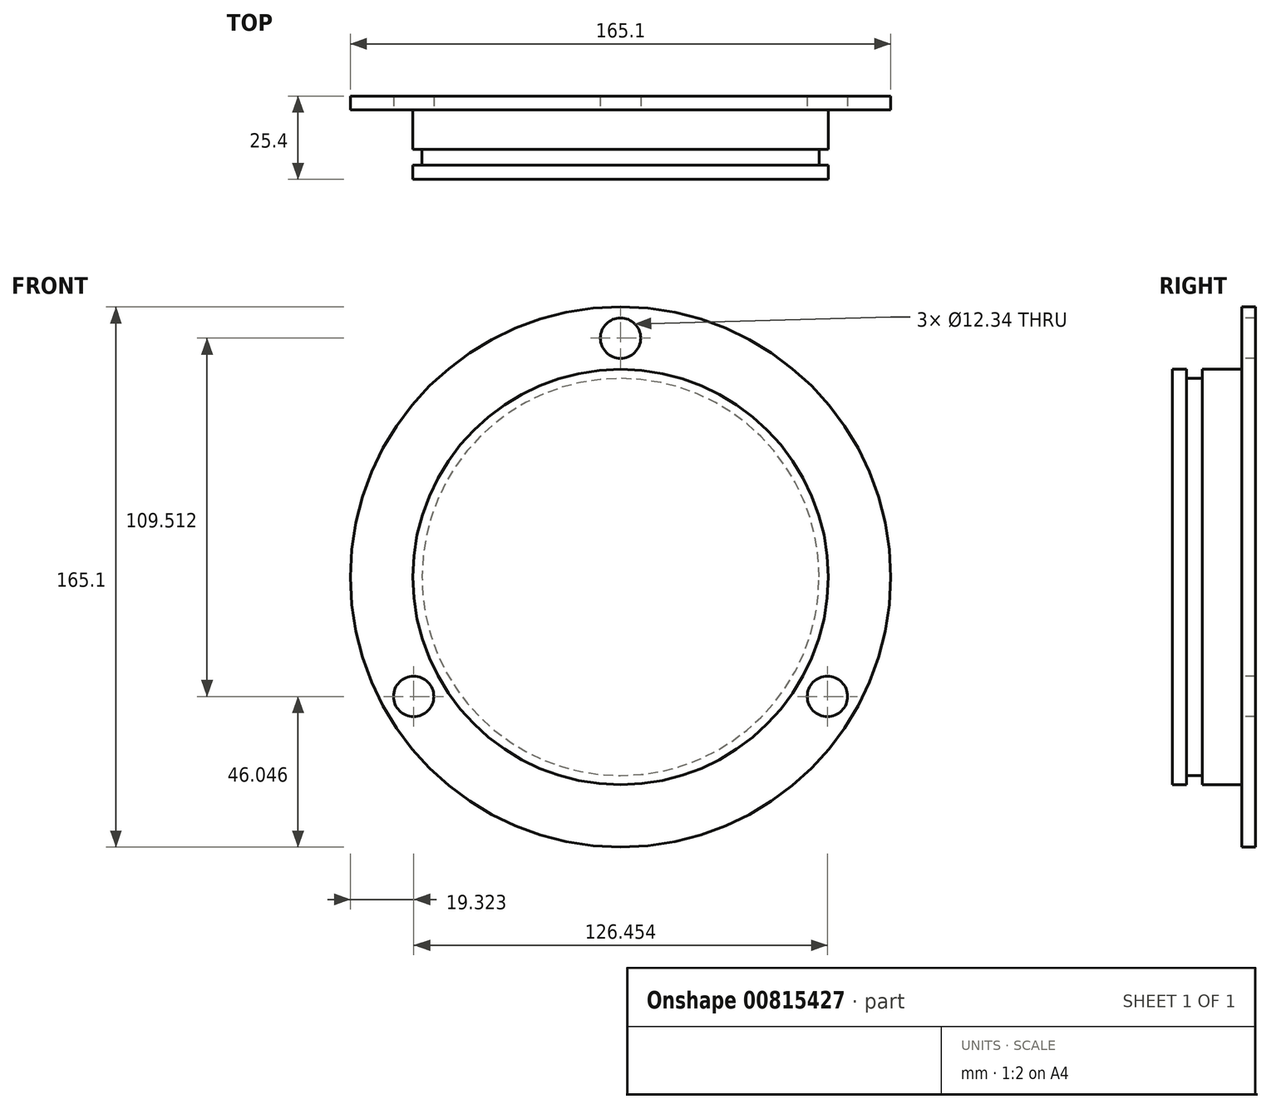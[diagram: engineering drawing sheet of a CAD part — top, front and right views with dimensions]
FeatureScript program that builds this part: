
annotation { "Feature Type Name" : "Feature", "Feature Type Description" : "" }
export const myFeature = defineFeature(function(context is Context, id is Id, definition is map)
    precondition{}
    {
        {
            var Q0;
            Q0=qCreatedBy(makeId("Front.planeOp"),FACE);
            var sketch = newSketch(context, id + "F0", { "sketchPlane" : qUnion([Q0])});
            skCircle(sketch, "E0", {"center": v(0, 0) * mm, "radius": 63.46 * mm});
            skSolve(sketch);
        }
        {
            var Q0;
            Q0=makeQuery(id+"F0.imprint","IMPRINT",FACE,{"disambiguationData":[TD([[makeQuery(id+"F0.imprint","IMPRINT",EDGE,{"derivedFrom":sQuery(id+"F0.wireOp",EDGE,"E0")}),1.0]])]});
            var Q1;
            Q1=sQuery(id+"F0.wireOp",EDGE,"E0");
            extrude(context, id + "F1", {"entities" : qUnion([Q0]), "surfaceEntities" : qUnion([Q1]), "depth" : 25.4 * mm, "offsetDistance" : 25.4 * mm});
        }
        {
            var Q0;
            Q0=makeQuery(id+"F1.opExtrude","SWEPT_BODY",BODY,{"disambiguationData":[OSD([sQuery(id+"F0.wireOp",EDGE,"E0")])]});
            var Q1;
            Q1=makeQuery(id+"F1.opExtrude","SWEPT_FACE",FACE,{"disambiguationData":[OSD([sQuery(id+"F0.wireOp",EDGE,"E0")])]});
            transform(context, id + "F2", {"entities" : qUnion([Q0]), "transformType" : TransformType.TRANSLATION_DISTANCE, "transformDirection" : qUnion([Q1]), "distance" : 27.79 * mm, "oppositeDirection" : true, "makeCopy" : false});
        }
        {
            var Q0;
            Q0=qCreatedBy(makeId("Right.planeOp"),FACE);
            var sketch = newSketch(context, id + "F3", { "sketchPlane" : qUnion([Q0])});
            skLineSegment(sketch, "E1.bottom", {"start": v(-27.79, 62.84) * mm, "end": v(-31.95, 62.84) * mm});
            skLineSegment(sketch, "E1.top", {"start": v(-27.79, 82.55) * mm, "end": v(-31.95, 82.55) * mm});
            skLineSegment(sketch, "E1.left", {"start": v(-27.79, 62.84) * mm, "end": v(-27.79, 82.55) * mm});
            skLineSegment(sketch, "E1.right", {"start": v(-31.95, 62.84) * mm, "end": v(-31.95, 82.55) * mm});
            skSolve(sketch);
        }
        {
            var Q0;
            Q0=qSketchRegion(id+"F3",true);
            var Q1;
            Q1=makeQuery(id+"F1.opExtrude","CAP_EDGE",EDGE,{"disambiguationData":[OSD([sQuery(id+"F0.wireOp",EDGE,"E0")])],"isStart":true});
            revolve(context, id + "F4", {"operationType" : NewBodyOperationType.ADD, "surfaceOperationType" : NewSurfaceOperationType.NEW, "entities" : qUnion([Q0]), "axis" : qUnion([Q1]), "revolveType" : RevolveType.FULL});
        }
        {
            var Q0;
            Q0=qCreatedBy(makeId("Right.planeOp"),FACE);
            var sketch = newSketch(context, id + "F5", { "sketchPlane" : qUnion([Q0])});
            skLineSegment(sketch, "E2", {"start": v(-141.55, -100.43) * mm, "end": v(-146.3, -100.43) * mm});
            skLineSegment(sketch, "E3.bottom", {"start": v(-146.3, -100.43) * mm, "end": v(-141.55, -100.43) * mm});
            skLineSegment(sketch, "E3.top", {"start": v(-146.3, -103.21) * mm, "end": v(-141.55, -103.21) * mm});
            skLineSegment(sketch, "E3.left", {"start": v(-146.3, -100.43) * mm, "end": v(-146.3, -103.21) * mm});
            skLineSegment(sketch, "E3.right", {"start": v(-141.55, -100.43) * mm, "end": v(-141.55, -103.21) * mm});
            skLineSegment(sketch, "E4", {"start": v(-44.07, 63.46) * mm, "end": v(-48.82, 63.46) * mm});
            skLineSegment(sketch, "E5.bottom", {"start": v(-48.82, 63.46) * mm, "end": v(-44.07, 63.46) * mm});
            skLineSegment(sketch, "E5.top", {"start": v(-48.82, 60.68) * mm, "end": v(-44.07, 60.68) * mm});
            skLineSegment(sketch, "E5.left", {"start": v(-48.82, 63.46) * mm, "end": v(-48.82, 60.68) * mm});
            skLineSegment(sketch, "E5.right", {"start": v(-44.07, 63.46) * mm, "end": v(-44.07, 60.68) * mm});
            skSolve(sketch);
        }
        {
            var Q0;
            Q0 = qSketchRegion(id + "F5", true);
            var Q1;
            Q1=makeQuery(id+"F1.opExtrude","SWEPT_FACE",FACE,{"disambiguationData":[OSD([sQuery(id+"F0.wireOp",EDGE,"E0")])]});
            revolve(context, id + "F6", {"operationType" : NewBodyOperationType.REMOVE, "surfaceOperationType" : NewSurfaceOperationType.NEW, "entities" : qUnion([Q0]), "axis" : qUnion([Q1]), "revolveType" : RevolveType.FULL, "oppositeDirection" : true});
        }
        {
            var Q0;
            Q0=makeQuery(id+"F4.opRevolve","SWEPT_FACE",FACE,{"disambiguationData":[OSD([sQuery(id+"F3.wireOp",EDGE,"E1.right")])]});
            var sketch = newSketch(context, id + "F7", { "sketchPlane" : qUnion([Q0])});
            skCircle(sketch, "E6", {"center": v(0, 73) * mm, "radius": 6.17 * mm});
            skCircle(sketch, "E7.1.0", {"center": v(-63.23, -36.5) * mm, "radius": 6.17 * mm});
            skCircle(sketch, "E7.2.0", {"center": v(63.23, -36.5) * mm, "radius": 6.17 * mm});
            skPoint(sketch, "E7.center", {"position": v(0, 0) * mm});
            skSolve(sketch);
        }
        {
            var Q0;
            Q0 = qSketchRegion(id + "F7", true);
            extrude(context, id + "F8", {"entities" : qUnion([Q0]), "operationType" : NewBodyOperationType.REMOVE, "oppositeDirection" : true, "depth" : 4.17 * mm, "offsetDistance" : 25.4 * mm});
        }
    });
